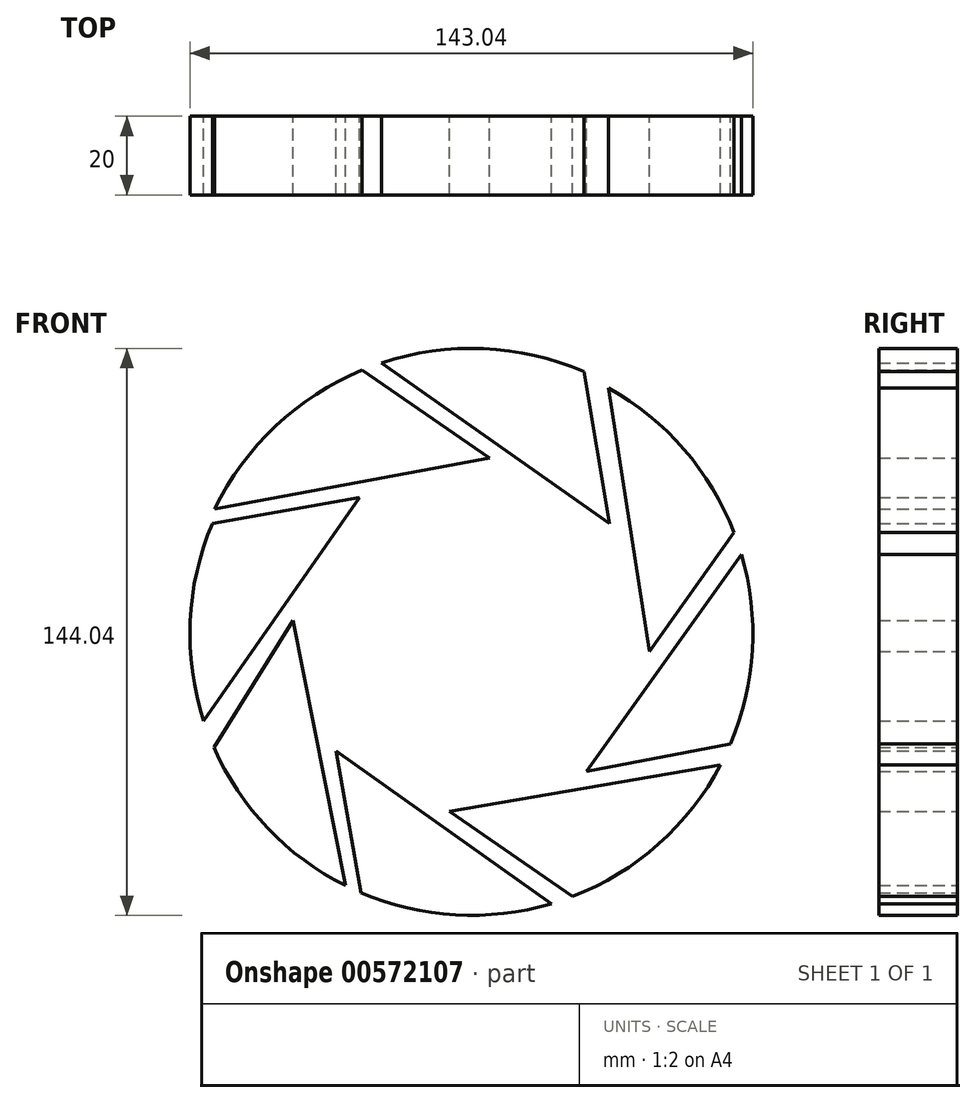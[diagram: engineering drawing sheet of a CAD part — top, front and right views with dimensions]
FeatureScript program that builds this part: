
annotation { "Feature Type Name" : "Feature", "Feature Type Description" : "" }
export const myFeature = defineFeature(function(context is Context, id is Id, definition is map)
    precondition{}
    {
        {
            var Q0;
            Q0=qCreatedBy(makeId("Front.planeOp"),FACE);
            var sketch = newSketch(context, id + "F0", { "sketchPlane" : qUnion([Q0])});
            skLineSegment(sketch, "E0", {"start": v(-65.22, 31.7) * mm, "end": v(4.63, 44.7) * mm});
            skArc(sketch, "E1", {"start": v(-27.83, 66.97) * mm, "mid": v(-49.76, 52.76) * mm, "end": v(-65.22, 31.7) * mm});
            skLineSegment(sketch, "E2", {"start": v(-27.83, 66.97) * mm, "end": v(4.63, 44.7) * mm});
            skSolve(sketch);
        }
        {
            var Q0;
            Q0=qCreatedBy(makeId("Front.planeOp"),FACE);
            var sketch = newSketch(context, id + "F1", { "sketchPlane" : qUnion([Q0])});
            skLineSegment(sketch, "E3", {"start": v(-22.86, 68.82) * mm, "end": v(35.12, 28.04) * mm});
            skArc(sketch, "E4", {"start": v(28.56, 66.66) * mm, "mid": v(3.05, 72.46) * mm, "end": v(-22.86, 68.82) * mm});
            skLineSegment(sketch, "E5", {"start": v(28.56, 66.66) * mm, "end": v(35.12, 28.04) * mm});
            skSolve(sketch);
        }
        {
            var Q0;
            Q0=qCreatedBy(makeId("Front.planeOp"),FACE);
            var sketch = newSketch(context, id + "F2", { "sketchPlane" : qUnion([Q0])});
            skLineSegment(sketch, "E6", {"start": v(34.89, 62.43) * mm, "end": v(45.25, -4.43) * mm});
            skArc(sketch, "E7", {"start": v(66.73, 25.75) * mm, "mid": v(54.02, 46.88) * mm, "end": v(34.89, 62.43) * mm});
            skLineSegment(sketch, "E8", {"start": v(66.73, 25.75) * mm, "end": v(45.25, -4.43) * mm});
            skSolve(sketch);
        }
        {
            var Q0;
            Q0=qCreatedBy(makeId("Front.planeOp"),FACE);
            var sketch = newSketch(context, id + "F3", { "sketchPlane" : qUnion([Q0])});
            skLineSegment(sketch, "E9", {"start": v(68.61, 20.19) * mm, "end": v(29.27, -34.9) * mm});
            skArc(sketch, "E10", {"start": v(65.83, -27.96) * mm, "mid": v(71.4, -4.13) * mm, "end": v(68.61, 20.19) * mm});
            skLineSegment(sketch, "E11", {"start": v(65.83, -27.96) * mm, "end": v(29.27, -34.9) * mm});
            skSolve(sketch);
        }
        {
            var Q0;
            Q0=qCreatedBy(makeId("Front.planeOp"),FACE);
            var sketch = newSketch(context, id + "F4", { "sketchPlane" : qUnion([Q0])});
            skLineSegment(sketch, "E12", {"start": v(63.32, -33.25) * mm, "end": v(-5.53, -45.07) * mm});
            skArc(sketch, "E13", {"start": v(25.75, -66.73) * mm, "mid": v(47.58, -53.4) * mm, "end": v(63.32, -33.25) * mm});
            skLineSegment(sketch, "E14", {"start": v(25.75, -66.73) * mm, "end": v(-5.53, -45.07) * mm});
            skSolve(sketch);
        }
        {
            var Q0;
            Q0=qCreatedBy(makeId("Front.planeOp"),FACE);
            var sketch = newSketch(context, id + "F5", { "sketchPlane" : qUnion([Q0])});
            skLineSegment(sketch, "E15", {"start": v(20.34, -68.57) * mm, "end": v(-34.37, -29.69) * mm});
            skArc(sketch, "E16", {"start": v(-28, -65.82) * mm, "mid": v(-4.07, -71.4) * mm, "end": v(20.34, -68.57) * mm});
            skLineSegment(sketch, "E17", {"start": v(-28, -65.82) * mm, "end": v(-34.37, -29.69) * mm});
            skSolve(sketch);
        }
        {
            var Q0;
            Q0=qCreatedBy(makeId("Front.planeOp"),FACE);
            var sketch = newSketch(context, id + "F6", { "sketchPlane" : qUnion([Q0])});
            skLineSegment(sketch, "E18", {"start": v(-32, -63.96) * mm, "end": v(-45.26, 3.45) * mm});
            skArc(sketch, "E19", {"start": v(-65.41, -28.92) * mm, "mid": v(-51.76, -49.35) * mm, "end": v(-32, -63.96) * mm});
            skLineSegment(sketch, "E20", {"start": v(-65.41, -28.92) * mm, "end": v(-45.26, 3.45) * mm});
            skSolve(sketch);
        }
        {
            var Q0;
            Q0=qCreatedBy(makeId("Front.planeOp"),FACE);
            var sketch = newSketch(context, id + "F7", { "sketchPlane" : qUnion([Q0])});
            skLineSegment(sketch, "E21", {"start": v(-68, -22.15) * mm, "end": v(-28.4, 34.63) * mm});
            skArc(sketch, "E22", {"start": v(-65.79, 28.06) * mm, "mid": v(-71.45, 3.16) * mm, "end": v(-68, -22.15) * mm});
            skLineSegment(sketch, "E23", {"start": v(-65.79, 28.06) * mm, "end": v(-28.4, 34.63) * mm});
            skSolve(sketch);
        }
        {
            var Q0;
            Q0=makeQuery(id+"F1.imprint","IMPRINT",FACE,{"disambiguationData":[TD([[makeQuery(id+"F1.imprint","IMPRINT",EDGE,{"derivedFrom":sQuery(id+"F1.wireOp",EDGE,"E3")}),1.0]])]});
            var Q1;
            Q1=makeQuery(id+"F0.imprint","IMPRINT",FACE,{"disambiguationData":[TD([[makeQuery(id+"F0.imprint","IMPRINT",EDGE,{"derivedFrom":sQuery(id+"F0.wireOp",EDGE,"E0")}),1.0]])]});
            var Q2;
            Q2=makeQuery(id+"F7.imprint","IMPRINT",FACE,{"disambiguationData":[TD([[makeQuery(id+"F7.imprint","IMPRINT",EDGE,{"derivedFrom":sQuery(id+"F7.wireOp",EDGE,"E21")}),1.0]])]});
            var Q3;
            Q3=makeQuery(id+"F6.imprint","IMPRINT",FACE,{"disambiguationData":[TD([[makeQuery(id+"F6.imprint","IMPRINT",EDGE,{"derivedFrom":sQuery(id+"F6.wireOp",EDGE,"E18")}),1.0]])]});
            var Q4;
            Q4=makeQuery(id+"F5.imprint","IMPRINT",FACE,{"disambiguationData":[TD([[makeQuery(id+"F5.imprint","IMPRINT",EDGE,{"derivedFrom":sQuery(id+"F5.wireOp",EDGE,"E15")}),1.0]])]});
            var Q5;
            Q5=makeQuery(id+"F4.imprint","IMPRINT",FACE,{"disambiguationData":[TD([[makeQuery(id+"F4.imprint","IMPRINT",EDGE,{"derivedFrom":sQuery(id+"F4.wireOp",EDGE,"E12")}),1.0]])]});
            var Q6;
            Q6=makeQuery(id+"F3.imprint","IMPRINT",FACE,{"disambiguationData":[TD([[makeQuery(id+"F3.imprint","IMPRINT",EDGE,{"derivedFrom":sQuery(id+"F3.wireOp",EDGE,"E9")}),1.0]])]});
            var Q7;
            Q7=makeQuery(id+"F2.imprint","IMPRINT",FACE,{"disambiguationData":[TD([[makeQuery(id+"F2.imprint","IMPRINT",EDGE,{"derivedFrom":sQuery(id+"F2.wireOp",EDGE,"E6")}),1.0]])]});
            var Q8;
            Q8=makeQuery(id+"F4.imprint","IMPRINT",FACE,{"disambiguationData":[TD([[makeQuery(id+"F4.imprint","IMPRINT",EDGE,{"derivedFrom":sQuery(id+"F4.wireOp",EDGE,"E12")}),1.0]])]});
            extrude(context, id + "F8", {"entities" : qUnion([Q0, Q1, Q2, Q3, Q4, Q5, Q6, Q7, Q8]), "depth" : 20 * mm, "offsetDistance" : 25 * mm});
        }
    });
